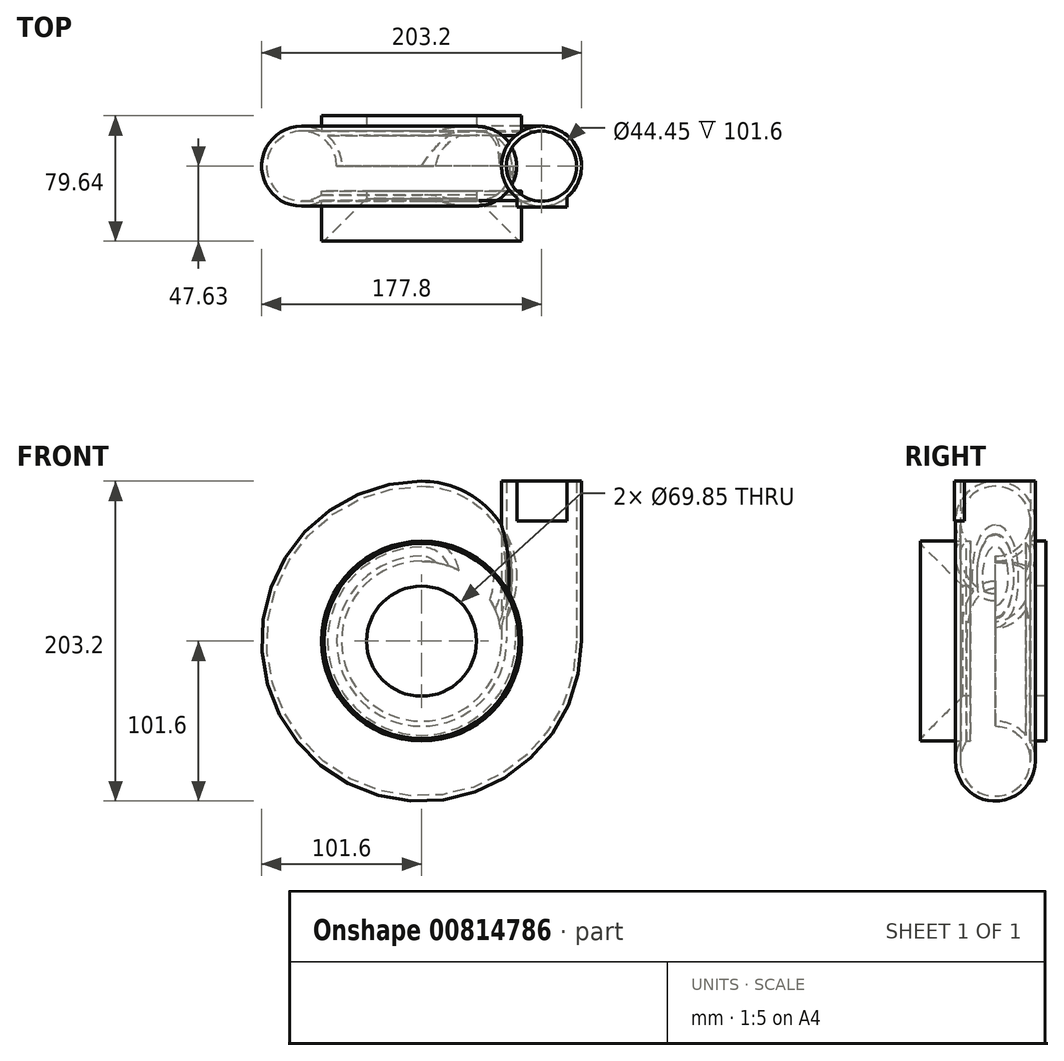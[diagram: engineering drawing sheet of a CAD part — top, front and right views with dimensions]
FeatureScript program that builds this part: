
annotation { "Feature Type Name" : "Feature", "Feature Type Description" : "" }
export const myFeature = defineFeature(function(context is Context, id is Id, definition is map)
    precondition{}
    {
        {
            var Q0;
            Q0=qCreatedBy(makeId("Front.planeOp"),FACE);
            var sketch = newSketch(context, id + "F0", { "sketchPlane" : qUnion([Q0])});
            skCircle(sketch, "E0", {"center": v(0, 0) * mm, "radius": 38.1 * mm});
            skCircle(sketch, "E1", {"center": v(0, 0) * mm, "radius": 50.8 * mm});
            skSolve(sketch);
        }
        {
            var Q0;
            Q0=qCreatedBy(makeId("Right.planeOp"),FACE);
            var sketch = newSketch(context, id + "F1", { "sketchPlane" : qUnion([Q0])});
            skCircle(sketch, "E2", {"center": v(0, 76.2) * mm, "radius": 25.4 * mm});
            skCircle(sketch, "E3", {"center": v(0, 76.2) * mm, "radius": 22.23 * mm});
            skSolve(sketch);
        }
        {
            var Q0;
            Q0=makeQuery(id+"F1.imprint","IMPRINT",FACE,{"disambiguationData":[TD([[makeQuery(id+"F1.imprint","IMPRINT",EDGE,{"derivedFrom":sQuery(id+"F1.wireOp",EDGE,"E2")}),1.0]])]});
            var Q1;
            Q1=sQuery(id+"F0.wireOp",EDGE,"E1");
            revolve(context, id + "F2", {"surfaceOperationType" : NewSurfaceOperationType.NEW, "entities" : qUnion([Q0]), "axis" : qUnion([Q1]), "revolveType" : RevolveType.ONE_DIRECTION, "angle" : 270 * degree});
        }
        {
            var Q0;
            Q0=makeQuery(id+"F2.opRevolve","CAP_FACE",FACE,{"disambiguationData":[OSD([sQuery(id+"F1.wireOp",EDGE,"E2"),sQuery(id+"F1.wireOp",EDGE,"E3")])],"isStart":false});
            extrude(context, id + "F3", {"entities" : qUnion([Q0]), "operationType" : NewBodyOperationType.ADD, "depth" : 101.6 * mm, "offsetDistance" : 25.4 * mm});
        }
        {
            var Q0;
            Q0=qCreatedBy(makeId("Front.planeOp"),FACE);
            var sketch = newSketch(context, id + "F4", { "sketchPlane" : qUnion([Q0])});
            skCircle(sketch, "E4", {"center": v(0, 41.28) * mm, "radius": 9.53 * mm, "construction": true});
            skSolve(sketch);
        }
        {
            var Q0;
            Q0=makeQuery(id+"F1.imprint","IMPRINT",FACE,{"disambiguationData":[TD([[makeQuery(id+"F1.imprint","IMPRINT",EDGE,{"derivedFrom":sQuery(id+"F1.wireOp",EDGE,"E2")}),1.0]])]});
            var Q1;
            Q1=sQuery(id+"F4.wireOp",EDGE,"E4");
            revolve(context, id + "F5", {"operationType" : NewBodyOperationType.ADD, "surfaceOperationType" : NewSurfaceOperationType.NEW, "entities" : qUnion([Q0]), "axis" : qUnion([Q1]), "revolveType" : RevolveType.ONE_DIRECTION, "oppositeDirection" : true, "angle" : 129.12 * degree});
        }
        {
            var Q0;
            Q0=sQuery(id+"F0.wireOp",VERTEX,"E1.center");
            var Q1;
            Q1=makeQuery(id+"F2.opRevolve","SWEPT_BODY",BODY,{"disambiguationData":[OSD([sQuery(id+"F1.wireOp",EDGE,"E2"),sQuery(id+"F1.wireOp",EDGE,"E3")])]});
            hole(context, id + "F6", {"style" : HoleStyle.SIMPLE, "endStyle" : HoleEndStyle.THROUGH, "holeDiameter" : 101.6 * mm, "majorDiameter" : 6.35 * mm, "isTappedThrough" : true, "tappedDepth" : 12.7 * mm, "tapClearance" : 3, "locations" : qUnion([Q0]), "scope" : qUnion([Q1])});
        }
        {
            var Q0;
            Q0=sQuery(id+"F0.wireOp",VERTEX,"E1.center");
            var Q1;
            Q1=makeQuery(id+"F2.opRevolve","SWEPT_BODY",BODY,{"disambiguationData":[OSD([sQuery(id+"F1.wireOp",EDGE,"E2"),sQuery(id+"F1.wireOp",EDGE,"E3")])]});
            hole(context, id + "F7", {"style" : HoleStyle.SIMPLE, "endStyle" : HoleEndStyle.THROUGH, "oppositeDirection" : true, "holeDiameter" : 127 * mm, "majorDiameter" : 6.35 * mm, "isTappedThrough" : true, "tappedDepth" : 12.7 * mm, "tapClearance" : 3, "locations" : qUnion([Q0]), "scope" : qUnion([Q1])});
        }
        {
            var Q0;
            Q0=makeQuery(id+"F0.imprint","IMPRINT",FACE,{"disambiguationData":[TD([[makeQuery(id+"F0.imprint","IMPRINT",EDGE,{"derivedFrom":sQuery(id+"F0.wireOp",EDGE,"E0")}),1.0]])]});
            cPlane(context, id + "F8", {"entities" : qUnion([Q0]), "cplaneType" : CPlaneType.OFFSET, "offset" : 15.88 * mm, "width" : 152.4 * mm, "height" : 152.4 * mm});
        }
        {
            var Q0;
            Q0=qCreatedBy(id+"F8.planeOp",FACE);
            var sketch = newSketch(context, id + "F9", { "sketchPlane" : qUnion([Q0])});
            skCircle(sketch, "E5", {"center": v(0, 0) * mm, "radius": 63.5 * mm});
            skSolve(sketch);
        }
        {
            var Q0;
            Q0=makeQuery(id+"F9.imprint","IMPRINT",FACE,{"disambiguationData":[TD([[makeQuery(id+"F9.imprint","IMPRINT",EDGE,{"derivedFrom":sQuery(id+"F9.wireOp",EDGE,"E5")}),1.0]])]});
            extrude(context, id + "F10", {"entities" : qUnion([Q0]), "operationType" : NewBodyOperationType.ADD, "depth" : 31.75 * mm, "offsetDistance" : 25.4 * mm});
        }
        {
            var Q0;
            Q0=makeQuery(id+"F0.imprint","IMPRINT",FACE,{"disambiguationData":[TD([[makeQuery(id+"F0.imprint","IMPRINT",EDGE,{"derivedFrom":sQuery(id+"F0.wireOp",EDGE,"E0")}),-1.0]])]});
            cPlane(context, id + "F11", {"entities" : qUnion([Q0]), "cplaneType" : CPlaneType.OFFSET, "offset" : 19.3 * mm, "oppositeDirection" : true, "width" : 152.4 * mm, "height" : 152.4 * mm});
        }
        {
            var Q0;
            Q0=qCreatedBy(id+"F11.planeOp",FACE);
            var sketch = newSketch(context, id + "F12", { "sketchPlane" : qUnion([Q0])});
            skCircle(sketch, "E6", {"center": v(0, 0) * mm, "radius": 63.5 * mm});
            skSolve(sketch);
        }
        {
            var Q0;
            Q0=makeQuery(id+"F12.imprint","IMPRINT",FACE,{"disambiguationData":[TD([[makeQuery(id+"F12.imprint","IMPRINT",EDGE,{"derivedFrom":sQuery(id+"F12.wireOp",EDGE,"E6")}),1.0]])]});
            extrude(context, id + "F13", {"entities" : qUnion([Q0]), "operationType" : NewBodyOperationType.ADD, "oppositeDirection" : true, "depth" : 12.7 * mm, "offsetDistance" : 25.4 * mm});
        }
        {
            var Q0;
            Q0=makeQuery(id+"F10.opExtrude","CAP_FACE",FACE,{"disambiguationData":[OSD([sQuery(id+"F9.wireOp",EDGE,"E5")])],"isStart":false});
            var sketch = newSketch(context, id + "F14", { "sketchPlane" : qUnion([Q0])});
            skPoint(sketch, "E7", {"position": v(0, 0) * mm});
            skSolve(sketch);
        }
        {
            var Q0;
            Q0=sQuery(id+"F14.wireOp",VERTEX,"E7");
            var Q1;
            Q1=makeQuery(id+"F2.opRevolve","SWEPT_BODY",BODY,{"disambiguationData":[OSD([sQuery(id+"F1.wireOp",EDGE,"E2"),sQuery(id+"F1.wireOp",EDGE,"E3")])]});
            hole(context, id + "F15", {"style" : HoleStyle.C_SINK, "endStyle" : HoleEndStyle.THROUGH, "holeDiameter" : 69.85 * mm, "cSinkDiameter" : 123.82 * mm, "cSinkAngle" : 90 * degree, "majorDiameter" : 6.35 * mm, "isTappedThrough" : true, "tappedDepth" : 12.7 * mm, "tapClearance" : 3, "locations" : qUnion([Q0]), "scope" : qUnion([Q1])});
        }
        {
            var Q0;
            Q0=makeQuery(id+"F3.opExtrude","CAP_FACE",FACE,{"disambiguationData":[OSD([sQuery(id+"F1.wireOp",EDGE,"E2"),sQuery(id+"F1.wireOp",EDGE,"E3")])],"isStart":false});
            cPlane(context, id + "F16", {"entities" : qUnion([Q0]), "cplaneType" : CPlaneType.OFFSET, "offset" : 0 * mm, "width" : 152.4 * mm, "height" : 152.4 * mm});
        }
        {
            var Q0;
            Q0=qCreatedBy(id+"F16.planeOp",FACE);
            var sketch = newSketch(context, id + "F17", { "sketchPlane" : qUnion([Q0])});
            skLineSegment(sketch, "E8.bottom", {"start": v(92.23, -25.89) * mm, "end": v(60.48, -25.89) * mm});
            skLineSegment(sketch, "E8.top", {"start": v(92.23, -18.32) * mm, "end": v(60.48, -18.32) * mm});
            skLineSegment(sketch, "E8.left", {"start": v(92.23, -25.89) * mm, "end": v(92.23, -18.32) * mm});
            skLineSegment(sketch, "E8.right", {"start": v(60.48, -25.89) * mm, "end": v(60.48, -18.32) * mm});
            skPoint(sketch, "E8.middle", {"position": v(76.36, -22.1) * mm});
            skCircle(sketch, "E9", {"center": v(76.09, -0.08) * mm, "radius": 25.25 * mm});
            skSolve(sketch);
        }
        {
            var Q0;
            {var subQ0=sQuery(id+"F17.wireOp",EDGE,"E8.bottom");Q0=makeQuery(id+"F17.imprint","IMPRINT",FACE,{"disambiguationData":[TD([[makeQuery(id+"F17.imprint","IMPRINT",EDGE,{"derivedFrom":subQ0}),-1.0]])]});}
            extrude(context, id + "F18", {"entities" : qUnion([Q0]), "operationType" : NewBodyOperationType.ADD, "oppositeDirection" : true, "depth" : 25.4 * mm, "offsetDistance" : 25.4 * mm});
        }
    });
